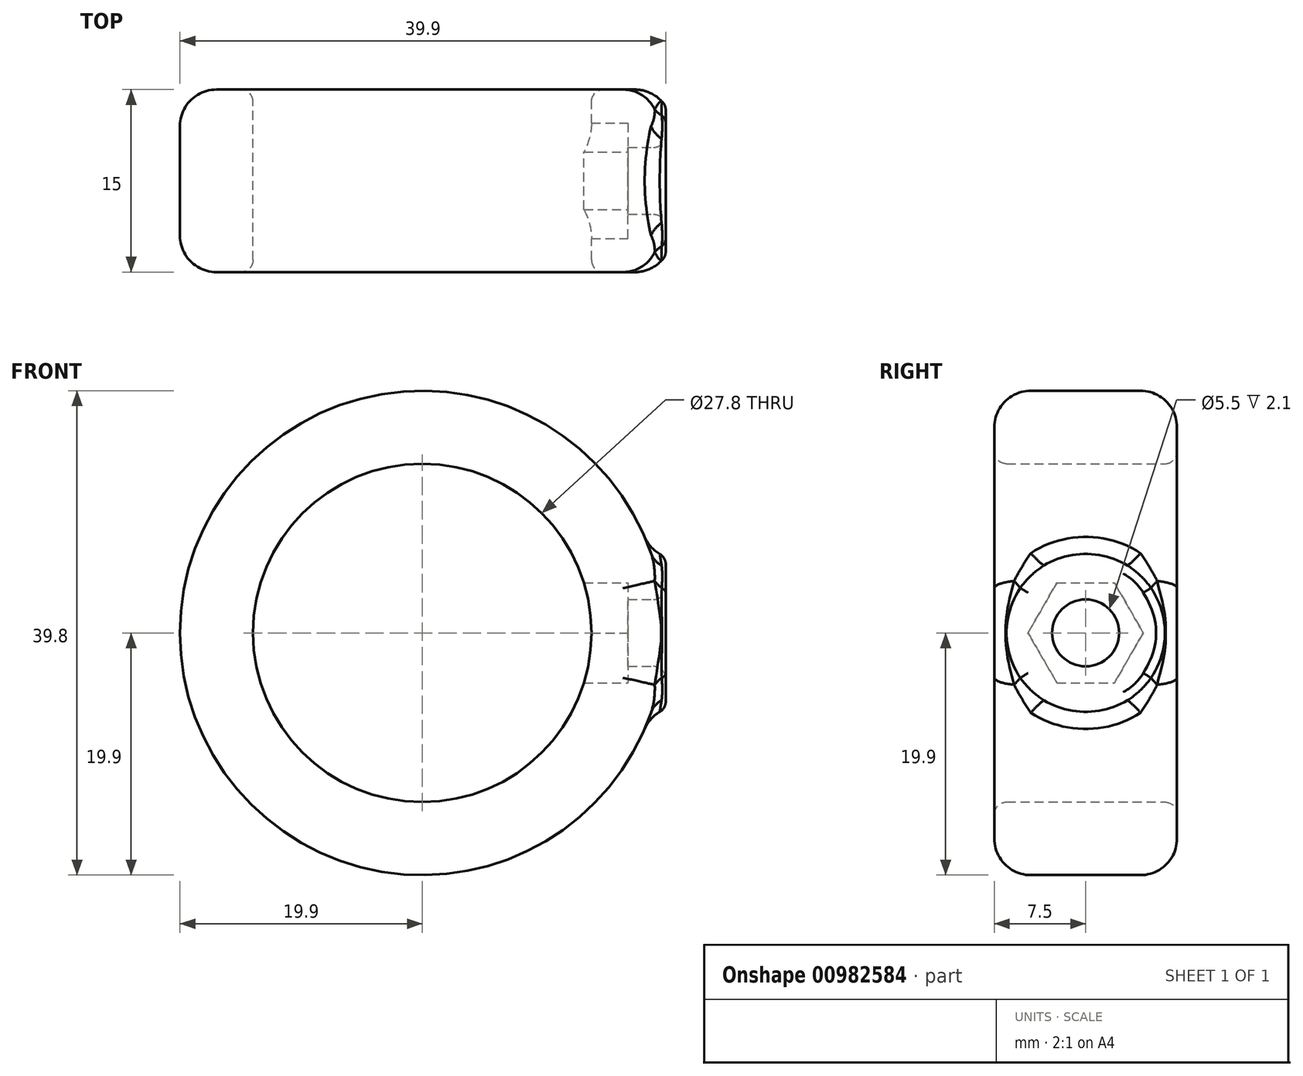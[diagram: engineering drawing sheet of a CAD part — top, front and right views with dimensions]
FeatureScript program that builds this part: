
annotation { "Feature Type Name" : "Feature", "Feature Type Description" : "" }
export const myFeature = defineFeature(function(context is Context, id is Id, definition is map)
    precondition{}
    {
        {
            var Q0;
            Q0=qCreatedBy(makeId("Front.planeOp"),FACE);
            var sketch = newSketch(context, id + "F0", { "sketchPlane" : qUnion([Q0])});
            skCircle(sketch, "E0", {"center": v(0, 0) * mm, "radius": 13.9 * mm});
            skCircle(sketch, "E1", {"center": v(0, 0) * mm, "radius": 19.9 * mm});
            skSolve(sketch);
        }
        {
            var Q0;
            Q0=qCreatedBy(makeId("Right.planeOp"),FACE);
            var sketch = newSketch(context, id + "F1", { "sketchPlane" : qUnion([Q0])});
            skCircle(sketch, "E2", {"center": v(0, 0) * mm, "radius": 6.25 * mm});
            skSolve(sketch);
        }
        {
            var Q0;
            Q0 = qSketchRegion(id + "F1", true);
            extrude(context, id + "F2", {"entities" : qUnion([Q0]), "depth" : 20 * mm, "offsetDistance" : 25 * mm});
        }
        {
            var Q0;
            Q0 = qSketchRegion(id + "F0", true);
            extrude(context, id + "F3", {"entities" : qUnion([Q0]), "operationType" : NewBodyOperationType.ADD, "endBound" : BoundingType.SYMMETRIC, "depth" : 15 * mm, "offsetDistance" : 25 * mm});
        }
        {
            var Q0;
            Q0=qCreatedBy(makeId("Front.planeOp"),FACE);
            var sketch = newSketch(context, id + "F4", { "sketchPlane" : qUnion([Q0])});
            skCircle(sketch, "E3", {"center": v(0, 0) * mm, "radius": 13.9 * mm});
            skSolve(sketch);
        }
        {
            var Q0;
            Q0 = qSketchRegion(id + "F4", true);
            extrude(context, id + "F5", {"entities" : qUnion([Q0]), "operationType" : NewBodyOperationType.REMOVE, "endBound" : BoundingType.SYMMETRIC, "depth" : 25 * mm, "offsetDistance" : 25 * mm});
        }
        {
            var Q0;
            Q0=qCreatedBy(makeId("Right.planeOp"),FACE);
            cPlane(context, id + "F6", {"entities" : qUnion([Q0]), "cplaneType" : CPlaneType.OFFSET, "offset" : 14.4 * mm, "width" : 150 * mm, "height" : 150 * mm});
        }
        {
            var Q0;
            Q0=qCreatedBy(id+"F6.planeOp",FACE);
            var sketch = newSketch(context, id + "F7", { "sketchPlane" : qUnion([Q0])});
            skCircle(sketch, "E4.cCircle", {"center": v(0, 0) * mm, "radius": 4.1 * mm, "construction": true});
            skLineSegment(sketch, "E4.0", {"start": v(2.37, -4.1) * mm, "end": v(-2.37, -4.1) * mm});
            skLineSegment(sketch, "E4.1", {"start": v(-2.37, -4.1) * mm, "end": v(-4.73, 0) * mm});
            skLineSegment(sketch, "E4.2", {"start": v(-4.73, 0) * mm, "end": v(-2.37, 4.1) * mm});
            skLineSegment(sketch, "E4.3", {"start": v(-2.37, 4.1) * mm, "end": v(2.37, 4.1) * mm});
            skLineSegment(sketch, "E4.4", {"start": v(2.37, 4.1) * mm, "end": v(4.73, 0) * mm});
            skLineSegment(sketch, "E4.5", {"start": v(4.73, 0) * mm, "end": v(2.37, -4.1) * mm});
            skPoint(sketch, "E4.0.midPoint", {"position": v(0, -4.1) * mm});
            skSolve(sketch);
        }
        {
            var Q0;
            Q0 = qSketchRegion(id + "F7", true);
            extrude(context, id + "F8", {"entities" : qUnion([Q0]), "operationType" : NewBodyOperationType.REMOVE, "endBound" : BoundingType.SYMMETRIC, "oppositeDirection" : true, "depth" : 5 * mm, "offsetDistance" : 25 * mm});
        }
        {
            var Q0;
            Q0=makeQuery(id+"F2.opExtrude","CAP_FACE",FACE,{"disambiguationData":[OSD([sQuery(id+"F1.wireOp",EDGE,"E2")])],"isStart":false});
            var sketch = newSketch(context, id + "F9", { "sketchPlane" : qUnion([Q0])});
            skCircle(sketch, "E5", {"center": v(0, 0) * mm, "radius": 2.75 * mm});
            skSolve(sketch);
        }
        {
            var Q0;
            Q0=makeQuery(id+"F9.imprint","IMPRINT",FACE,{"disambiguationData":[TD([[makeQuery(id+"F9.imprint","IMPRINT",EDGE,{"derivedFrom":sQuery(id+"F9.wireOp",EDGE,"E5")}),1.0]])]});
            extrude(context, id + "F10", {"entities" : qUnion([Q0]), "operationType" : NewBodyOperationType.REMOVE, "oppositeDirection" : true, "depth" : 25 * mm, "offsetDistance" : 25 * mm});
        }
        {
            var Q0;
            Q0=makeQuery(id+"F3.opExtrude","CAP_EDGE",EDGE,{"disambiguationData":[OSD([sQuery(id+"F0.wireOp",EDGE,"E0")])],"isStart":false});
            var Q1;
            Q1=makeQuery(id+"F3.opExtrude","CAP_EDGE",EDGE,{"disambiguationData":[OSD([sQuery(id+"F0.wireOp",EDGE,"E0")])],"isStart":true});
            fillet(context, id + "F11", {"entities" : qUnion([Q0, Q1]), "radius" : 1 * mm, "tangentPropagation" : true, "allowEdgeOverflow" : false});
        }
        {
            var Q0;
            Q0=makeQuery(id+"F3.opExtrude","CAP_EDGE",EDGE,{"disambiguationData":[OSD([sQuery(id+"F0.wireOp",EDGE,"E1")])],"isStart":false});
            var Q1;
            Q1=makeQuery(id+"F3.opExtrude","CAP_EDGE",EDGE,{"disambiguationData":[OSD([sQuery(id+"F0.wireOp",EDGE,"E1")])],"isStart":true});
            fillet(context, id + "F12", {"entities" : qUnion([Q0, Q1]), "radius" : 3 * mm, "tangentPropagation" : true, "allowEdgeOverflow" : false});
        }
        {
            var Q0;
            Q0=makeQuery(id+"F3.boolean.opBoolean","INTERSECT",EDGE,{"derivedFrom":[makeQuery(id+"F2.opExtrude","SWEPT_FACE",FACE,{"disambiguationData":[OSD([sQuery(id+"F1.wireOp",EDGE,"E2")])]}),makeQuery(id+"F3.opExtrude","SWEPT_FACE",FACE,{"disambiguationData":[OSD([sQuery(id+"F0.wireOp",EDGE,"E1")])]})]});
            fillet(context, id + "F13", {"entities" : qUnion([Q0]), "radius" : 3 * mm, "tangentPropagation" : true, "allowEdgeOverflow" : false});
        }
        {
            var Q0;
            Q0=makeQuery(id+"F2.opExtrude","CAP_FACE",FACE,{"disambiguationData":[OSD([sQuery(id+"F1.wireOp",EDGE,"E2")])],"isStart":false});
            fillet(context, id + "F14", {"entities" : qUnion([Q0]), "radius" : 1 * mm, "tangentPropagation" : true, "allowEdgeOverflow" : false});
        }
    });
